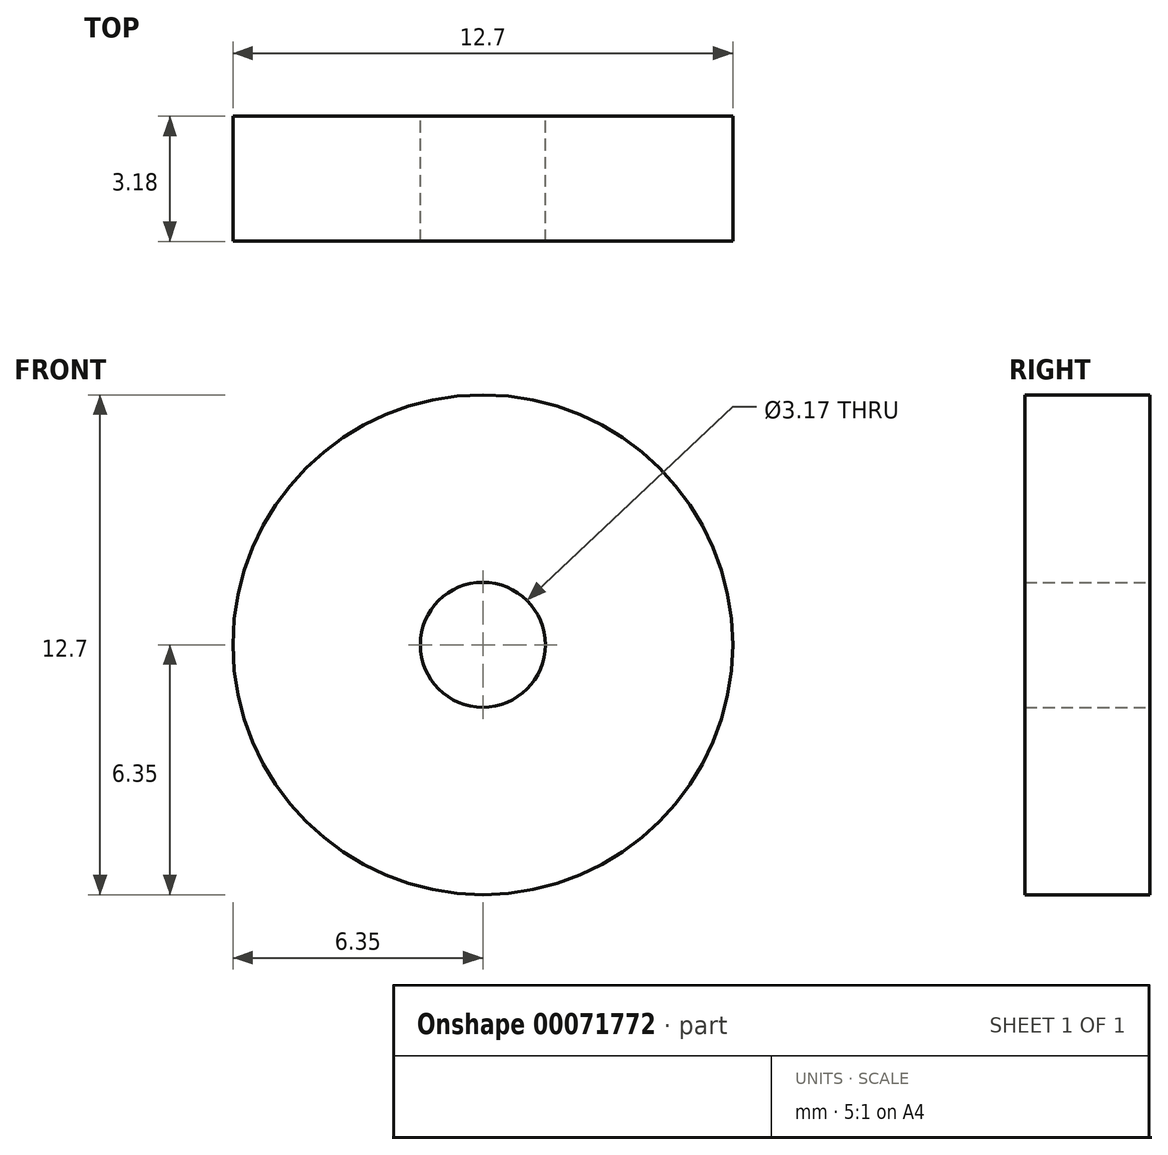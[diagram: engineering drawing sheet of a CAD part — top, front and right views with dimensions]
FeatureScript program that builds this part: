
annotation { "Feature Type Name" : "Feature", "Feature Type Description" : "" }
export const myFeature = defineFeature(function(context is Context, id is Id, definition is map)
    precondition{}
    {
        {
            var Q0;
            Q0=qCreatedBy(makeId("Front.planeOp"),FACE);
            var sketch = newSketch(context, id + "F0", { "sketchPlane" : qUnion([Q0])});
            skCircle(sketch, "E0", {"center": v(0, 0) * mm, "radius": 6.35 * mm});
            skCircle(sketch, "E1", {"center": v(0, 0) * mm, "radius": 1.59 * mm});
            skSolve(sketch);
        }
        {
            var Q0;
            Q0=makeQuery(id+"F0.imprint","IMPRINT",FACE,{"disambiguationData":[TD([[makeQuery(id+"F0.imprint","IMPRINT",EDGE,{"derivedFrom":sQuery(id+"F0.wireOp",EDGE,"E0")}),1.0]])]});
            extrude(context, id + "F1", {"entities" : qUnion([Q0]), "depth" : 3.17 * mm});
        }
    });
